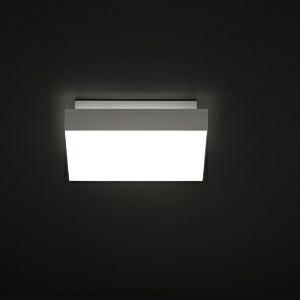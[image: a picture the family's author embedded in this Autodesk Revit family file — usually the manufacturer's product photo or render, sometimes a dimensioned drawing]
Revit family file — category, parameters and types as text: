
# Revit family: spectral_norea_norea-qa_422_5200_840_mps_0dc4
name_source: partatom
category: Lighting Fixtures
revit_build: Autodesk Revit 2016 (Build: 20150220_1215(x64)
units: mm (PartAtom-declared; Revit-internal decimal feet)

## family parameters
Cut with Voids When Loaded = No
Host = Face
Light Source = No
Part Type = Normal
Room Calculation Point = No
Round Connector Dimension = Use Diameter
Shared = No

## types (1)
- SPECTRAL NOREA (1 x )
    Apparent Load = 0 VA
    Approval mark = CE
    CIE Flux Codes = 69 93 98 98 73
    Control Gear = Electronic transformer
    Default Elevation = 1800 mm
    Description = SPT0000103
NOREA surface-mounted luminaire

Design:
Square luminaire element with a microprism panel in a natural anodised aluminium profile frame surround. The frame is suspended at the metal body. The LED module is formed as a square LED flat board and screwed to the luminaire element. For connection of the luminaire this can be hinged down and fastened with screws at an oblong hole in the powder-coated metal body. The indirect component is ensured by recesses in the top of the metal body. The metal body accommodates the electrical components and electronic ballast. Luminaire with heat-resistant wiring. Variant suitable for office use with a microprism panel MPS. The LED points are visible as circles on the microprism panel. Suitable for ceiling or wall mounting. Also in a dimmable version. Light colours 830 und 840. Protection rating IP20, safety class I.

Colour:
Housing – similar to RAL 9016 White silk matt;
Frame – natural anodised
    Height = 80 mm  [stored 0.262467 ft]
    Lamp = 1 x
    Lamp count = 1
    Length = 422 mm
    Luminous efficacy = 0 lm/W
    Manufacturer = Ridi
    ModVariant = No
    Model = NOREA-QA 422/5200/840 MPS
    Mounting Place = Ceiling
    Mounting Type = Surface mounted
    Number of Poles = 1
    OnlyDefault = Yes
    Power Factor = 1
    Product Name = SPECTRAL NOREA
    Product group = Ceiling mounted luminaire
    ProductGroupID = 3
    Protection Class = Protection class
    Protection Degree = IP 20
    RlxData = <blob elided: 31433 chars, md5=c9a8839a>
    Socket = socket
    Standby Power = 0 W
    System Light Flux = 0 lm
    System Power = 0 W
    Type Image = leuchtstoffklein02_-_kopie.jpg
    URL = http://reluxnet.relux.com
    VarID = 1
    Voltage = 0 V
    Weight = 0.00 kg
    Width = 422 mm

note: [stored X ft] marks values corroborated as IEEE doubles in the binary element streams (Revit-internal decimal feet)

## geometry (parser evidence)
native form markers: Blend x4, Sweep x12
no freeform markers — native parametric forms only
